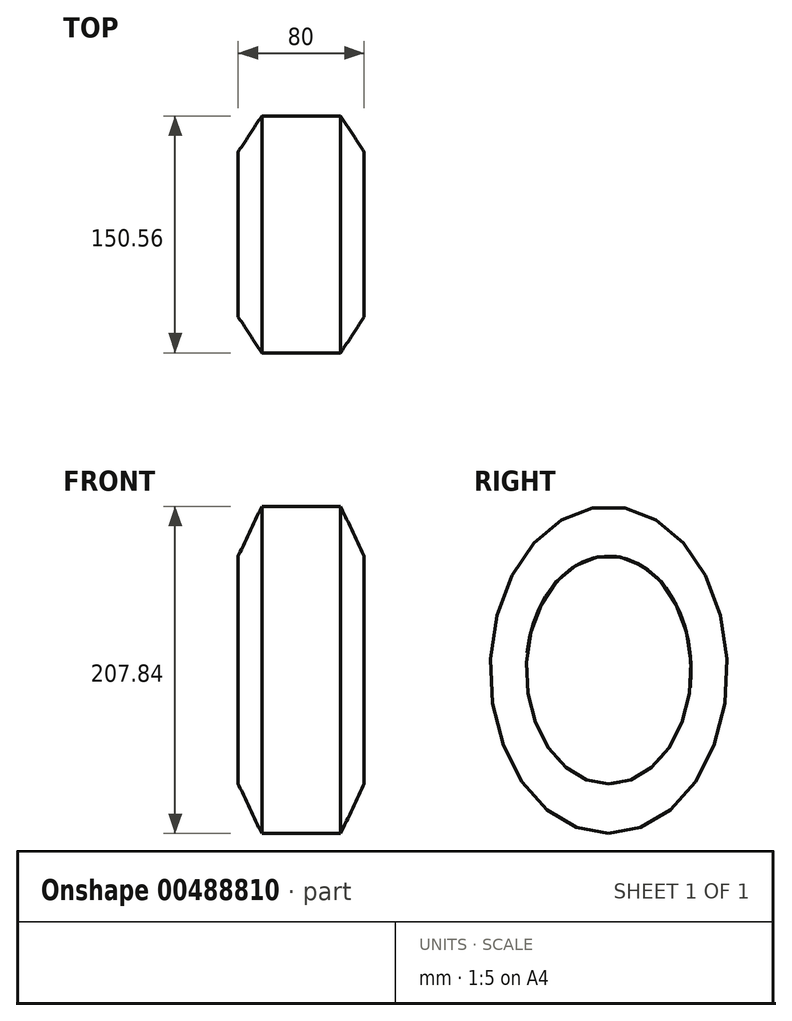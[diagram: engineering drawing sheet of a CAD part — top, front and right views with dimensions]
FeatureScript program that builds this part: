
annotation { "Feature Type Name" : "Feature", "Feature Type Description" : "" }
export const myFeature = defineFeature(function(context is Context, id is Id, definition is map)
    precondition{}
    {
        {
            var Q0;
            Q0=qCreatedBy(makeId("Right.planeOp"),FACE);
            var sketch = newSketch(context, id + "F0", { "sketchPlane" : qUnion([Q0])});
            skEllipse(sketch, "E0", {"center": v(0, 0) * mm, "majorRadius": 103.92 * mm, "minorRadius": 75.28 * mm, "majorAxis": v(0, -1)});
            skSolve(sketch);
        }
        {
            var Q0;
            Q0=qCreatedBy(makeId("Right.planeOp"),FACE);
            cPlane(context, id + "F1", {"entities" : qUnion([Q0]), "cplaneType" : CPlaneType.OFFSET, "offset" : 40 * mm, "width" : 150 * mm, "height" : 150 * mm});
        }
        {
            var Q0;
            Q0=qCreatedBy(makeId("Right.planeOp"),FACE);
            cPlane(context, id + "F2", {"entities" : qUnion([Q0]), "cplaneType" : CPlaneType.OFFSET, "offset" : 40 * mm, "oppositeDirection" : true, "width" : 150 * mm, "height" : 150 * mm});
        }
        {
            var Q0;
            Q0=qCreatedBy(id+"F1.planeOp",FACE);
            var sketch = newSketch(context, id + "F3", { "sketchPlane" : qUnion([Q0])});
            skEllipse(sketch, "E1", {"center": v(0, 0) * mm, "majorRadius": 72.35 * mm, "minorRadius": 52.4 * mm, "majorAxis": v(0, -1)});
            skSolve(sketch);
        }
        {
            var Q0;
            Q0=qCreatedBy(id+"F2.planeOp",FACE);
            var sketch = newSketch(context, id + "F4", { "sketchPlane" : qUnion([Q0])});
            skEllipse(sketch, "E2", {"center": v(0, 0) * mm, "majorRadius": 72.35 * mm, "minorRadius": 52.4 * mm, "majorAxis": v(0, -1)});
            skSolve(sketch);
        }
        {
            var Q0;
            Q0=sQuery(id+"F0.wireOp",EDGE,"E0");
            extrude(context, id + "F5", {"bodyType" : ToolBodyType.SURFACE, "surfaceEntities" : qUnion([Q0]), "depth" : 25 * mm, "hasSecondDirection" : true, "secondDirectionOppositeDirection" : true, "secondDirectionDepth" : 25 * mm});
        }
        {
            var Q0;
            Q0=sQuery(id+"F3.wireOp",EDGE,"E1");
            var Q1;
            Q1=makeQuery(id+"F5.opExtrude","CAP_EDGE",EDGE,{"disambiguationData":[OSD([sQuery(id+"F0.wireOp",EDGE,"E0")])],"isStart":false});
            loft(context, id + "F6", {"bodyType" : ToolBodyType.SURFACE, "wireProfilesArray" : [{ "wireProfileEntities" : qUnion([Q0]) }, { "wireProfileEntities" : qUnion([Q1]) }]});
        }
        {
            var Q0;
            Q0=makeQuery(id+"F5.opExtrude","CAP_EDGE",EDGE,{"disambiguationData":[OSD([sQuery(id+"F0.wireOp",EDGE,"E0")])],"isStart":true});
            var Q1;
            Q1=sQuery(id+"F4.wireOp",EDGE,"E2");
            loft(context, id + "F7", {"bodyType" : ToolBodyType.SURFACE, "wireProfilesArray" : [{ "wireProfileEntities" : qUnion([Q0]) }, { "wireProfileEntities" : qUnion([Q1]) }]});
        }
    });
